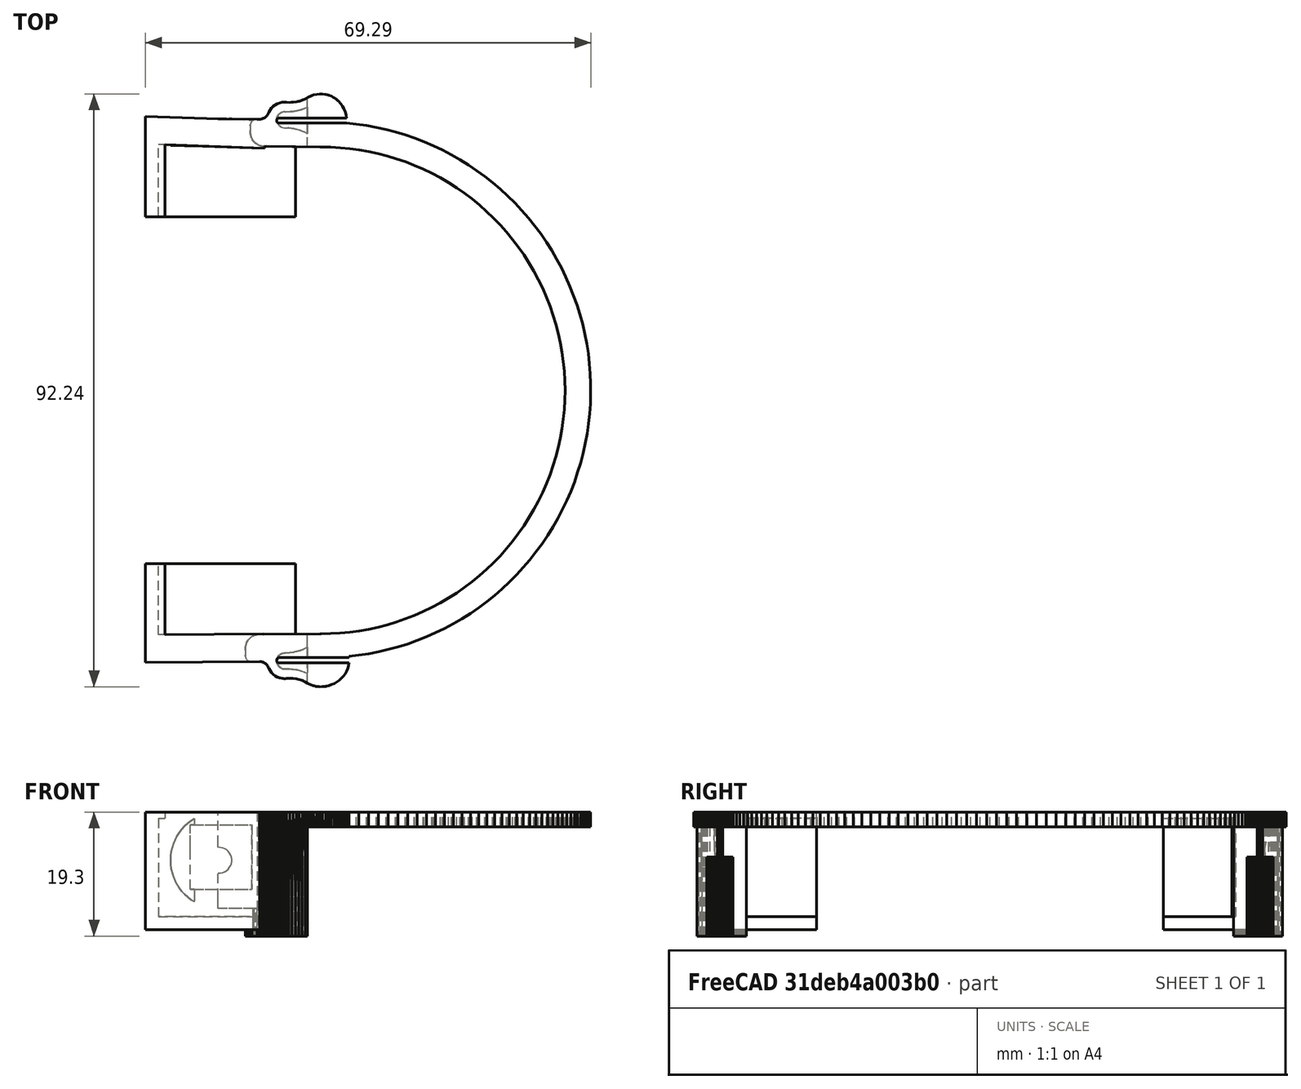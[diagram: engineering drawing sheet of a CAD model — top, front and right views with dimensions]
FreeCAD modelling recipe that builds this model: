
FCSTD DOCUMENT  (FreeCAD 0.18R4 (GitTag))
Label: test_antipop
License: All rights reserved
LicenseURL: http://en.wikipedia.org/wiki/All_rights_reserved
objects: Part::Box×2, Part::Cut×2, Part::Feature×1, Mesh::Feature×1
note: 5 computed .brp shape members not serialized (recipe doc carries the construction recipe); baked Part::Feature solids carry a one-line shape summary decoded from their .brp

FEATURE [Part::Feature] Cut049001  label="01-bracket-to_do_mesh001"
  shape: bbox 69.29 x 92.24 x 93 mm, 2259 faces (baked)
FEATURE [Part::Box] Box  label="Cube"
  AttacherType = Attacher::AttachEngine3D
  Height = 80
  Length = 60
  Placement = pos=(0,-50,-68) rot=(0,0,1;0rad)
  Width = 100
FEATURE [Part::Cut] Cut
  Base = -> Cut049001
  Refine = true
  Tool = -> Box
FEATURE [Part::Box] Box001  label="Cube001"
  AttacherType = Attacher::AttachEngine3D
  Height = 60
  Length = 60
  Placement = pos=(14,-50,-31) rot=(0,0,1;0rad)
  Width = 100
FEATURE [Part::Cut] Cut049002
  Base = -> Cut
  Refine = true
  Tool = -> Box001
FEATURE [Mesh::Feature] Mesh  label="Cut049002 (Meshed)"
